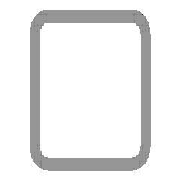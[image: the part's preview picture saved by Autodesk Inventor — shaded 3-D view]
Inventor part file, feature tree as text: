
AUTODESK INVENTOR PART (.ipt)
format: ipt  version: 2024 (Build 280153000, 153)  size: 153,088 bytes
history: native  units: mm (DEFAULTED — no unit token found)
features: other x4, plane x2, split x1, sketch x1
ambient origin geometry x8: Origin, YZ Plane, XZ Plane, XY Plane, X Axis, Y Axis, Z Axis, Center Point
bodies: Solid1 (feature_tree), Body (feature_tree)
feature tree (8):
  parser-record x1  (decoder bookkeeping rows leaked as tree rows — omitted from the tree; the rows remain in map.json)
  other  "Driven Length"
  other  "Start Plane"
  other  "End Plane"
  plane  "Work Plane6"
  split  "Split3"
  sketch  "Sketch3"  dims[d3=985.382863mm d4=0.0mm d7=7.5mm d10=100.0mm d11=100.0mm d12=5.0mm d13=24.117137mm d14=1009.5mm d15=50.0mm d16=50.0mm d17=90.0deg d18=985.382863mm d19=5.0mm d20=5.0mm]
  plane  "Work Plane3"
